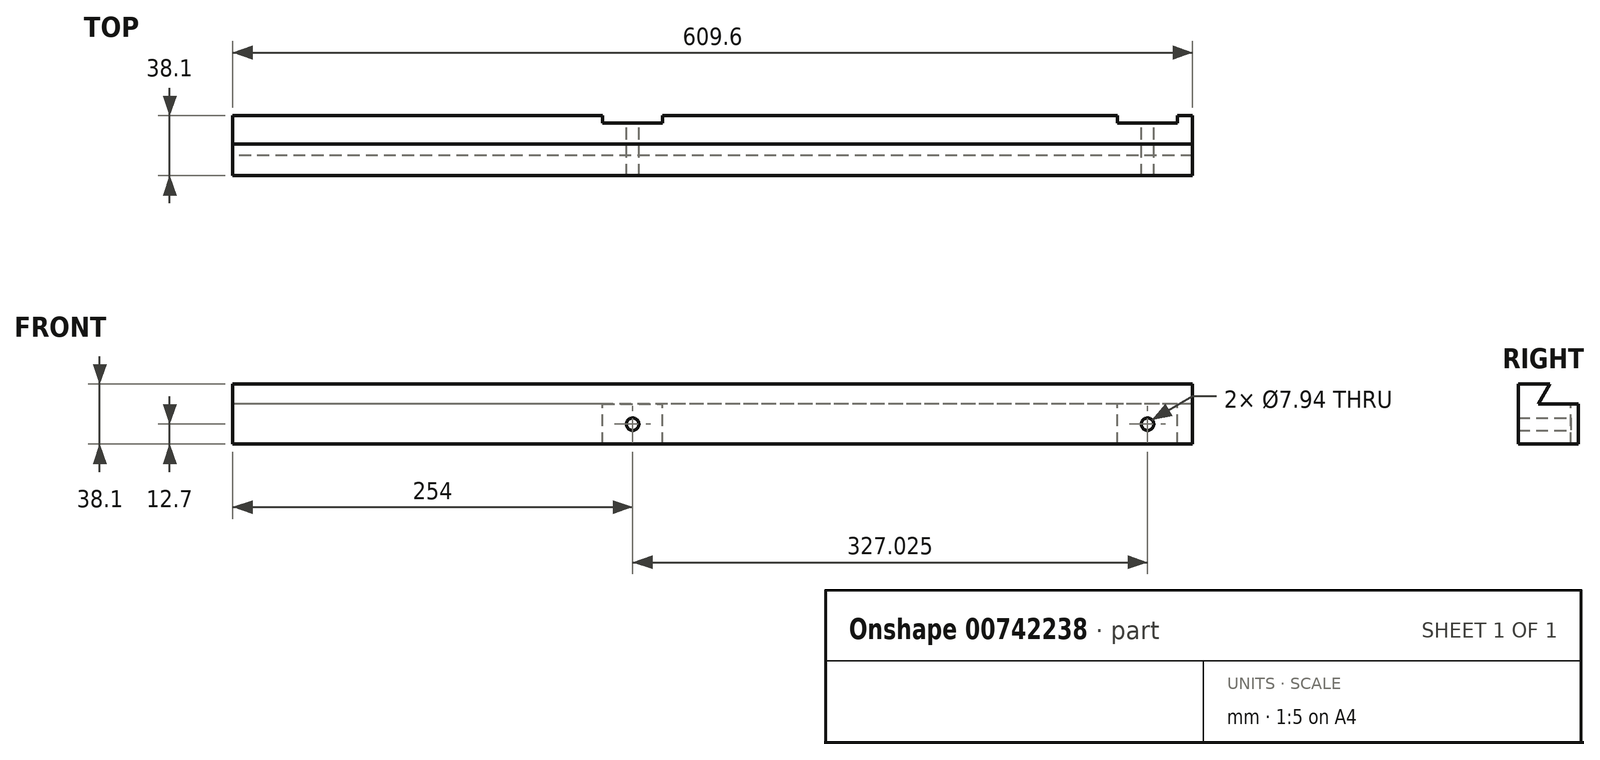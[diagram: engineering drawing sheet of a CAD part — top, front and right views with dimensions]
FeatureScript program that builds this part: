
annotation { "Feature Type Name" : "Feature", "Feature Type Description" : "" }
export const myFeature = defineFeature(function(context is Context, id is Id, definition is map)
    precondition{}
    {
        {
            var Q0;
            Q0=qCreatedBy(makeId("Right.planeOp"),FACE);
            var sketch = newSketch(context, id + "F0", { "sketchPlane" : qUnion([Q0])});
            skLineSegment(sketch, "E0", {"start": v(0, 0) * mm, "end": v(0, 38.1) * mm});
            skLineSegment(sketch, "E1", {"start": v(0, 38.1) * mm, "end": v(12.7, 38.1) * mm});
            skLineSegment(sketch, "E2", {"start": v(12.7, 38.1) * mm, "end": v(12.7, 25.4) * mm});
            skLineSegment(sketch, "E3", {"start": v(12.7, 25.4) * mm, "end": v(38.1, 25.4) * mm});
            skLineSegment(sketch, "E4", {"start": v(38.1, 25.4) * mm, "end": v(38.1, 0) * mm});
            skLineSegment(sketch, "E5", {"start": v(38.1, 0) * mm, "end": v(0, 0) * mm});
            skSolve(sketch);
        }
        {
            var Q0;
            Q0=makeQuery(id+"F0.imprint","IMPRINT",FACE,{"disambiguationData":[TD([[makeQuery(id+"F0.imprint","IMPRINT",EDGE,{"derivedFrom":sQuery(id+"F0.wireOp",EDGE,"E0")}),-1.0]])]});
            extrude(context, id + "F1", {"entities" : qUnion([Q0]), "depth" : 304.8 * mm, "offsetDistance" : 25.4 * mm, "hasSecondDirection" : true, "secondDirectionOppositeDirection" : true, "secondDirectionDepth" : 304.8 * mm});
        }
        {
            var Q0;
            Q0=makeQuery(id+"F1.opExtrude","SWEPT_FACE",FACE,{"disambiguationData":[OSD([sQuery(id+"F0.wireOp",EDGE,"E3")])]});
            var sketch = newSketch(context, id + "F2", { "sketchPlane" : qUnion([Q0])});
            skLineSegment(sketch, "E6", {"start": v(295.28, 38.1) * mm, "end": v(295.28, 33.34) * mm});
            skLineSegment(sketch, "E7", {"start": v(295.28, 33.34) * mm, "end": v(257.18, 33.34) * mm});
            skLineSegment(sketch, "E8", {"start": v(257.18, 33.34) * mm, "end": v(257.18, 38.1) * mm});
            skLineSegment(sketch, "E9", {"start": v(257.18, 38.1) * mm, "end": v(295.28, 38.1) * mm});
            skLineSegment(sketch, "E10", {"start": v(-69.85, 38.1) * mm, "end": v(-69.85, 33.34) * mm});
            skLineSegment(sketch, "E11", {"start": v(-69.85, 33.34) * mm, "end": v(-31.75, 33.34) * mm});
            skLineSegment(sketch, "E12", {"start": v(-31.75, 33.34) * mm, "end": v(-31.75, 38.1) * mm});
            skLineSegment(sketch, "E13", {"start": v(-31.75, 38.1) * mm, "end": v(-69.85, 38.1) * mm});
            skSolve(sketch);
        }
        {
            var Q0;
            Q0=makeQuery(id+"F2.imprint","IMPRINT",FACE,{"disambiguationData":[TD([[makeQuery(id+"F2.imprint","IMPRINT",EDGE,{"derivedFrom":sQuery(id+"F2.wireOp",EDGE,"E10")}),1.0]])]});
            var Q1;
            Q1=makeQuery(id+"F2.imprint","IMPRINT",FACE,{"disambiguationData":[TD([[makeQuery(id+"F2.imprint","IMPRINT",EDGE,{"derivedFrom":sQuery(id+"F2.wireOp",EDGE,"E6")}),-1.0]])]});
            extrude(context, id + "F3", {"entities" : qUnion([Q0, Q1]), "operationType" : NewBodyOperationType.REMOVE, "endBound" : BoundingType.THROUGH_ALL, "oppositeDirection" : true, "depth" : 25.4 * mm, "offsetDistance" : 25.4 * mm});
        }
        {
            var Q0;
            Q0=makeQuery(id+"F3.boolean.opBoolean","COPY",FACE,{"derivedFrom":makeQuery(id+"F3.opExtrude","SWEPT_FACE",FACE,{"disambiguationData":[OSD([sQuery(id+"F2.wireOp",EDGE,"E11")])]})});
            var sketch = newSketch(context, id + "F4", { "sketchPlane" : qUnion([Q0])});
            skPoint(sketch, "E14", {"position": v(-276.22, 12.7) * mm});
            skPoint(sketch, "E15", {"position": v(50.8, 12.7) * mm});
            skLineSegment(sketch, "E16", {"start": v(50.8, 25.4) * mm, "end": v(50.8, -27.74) * mm, "construction": true});
            skLineSegment(sketch, "E17", {"start": v(69.85, 12.7) * mm, "end": v(31.75, 12.7) * mm, "construction": true});
            skSolve(sketch);
        }
        {
            var Q0;
            Q0=sQuery(id+"F4.wireOp",VERTEX,"E14");
            var Q1;
            Q1=sQuery(id+"F4.wireOp",VERTEX,"E15");
            var Q2;
            Q2=makeQuery(id+"F1.opExtrude","SWEPT_BODY",BODY,{"disambiguationData":[OSD([sQuery(id+"F0.wireOp",EDGE,"E0"),sQuery(id+"F0.wireOp",EDGE,"E1"),sQuery(id+"F0.wireOp",EDGE,"E2"),sQuery(id+"F0.wireOp",EDGE,"E3"),sQuery(id+"F0.wireOp",EDGE,"E4"),sQuery(id+"F0.wireOp",EDGE,"E5")])]});
            hole(context, id + "F5", {"style" : HoleStyle.SIMPLE, "endStyle" : HoleEndStyle.THROUGH, "holeDiameter" : 7.94 * mm, "majorDiameter" : 6.35 * mm, "isTappedThrough" : true, "tappedDepth" : 12.7 * mm, "tapClearance" : 3, "locations" : qUnion([Q0, Q1]), "scope" : qUnion([Q2])});
        }
        {
            var Q0;
            Q0=makeQuery(id+"F1.opExtrude","CAP_FACE",FACE,{"disambiguationData":[OSD([sQuery(id+"F0.wireOp",EDGE,"E0"),sQuery(id+"F0.wireOp",EDGE,"E1"),sQuery(id+"F0.wireOp",EDGE,"E2"),sQuery(id+"F0.wireOp",EDGE,"E3"),sQuery(id+"F0.wireOp",EDGE,"E4"),sQuery(id+"F0.wireOp",EDGE,"E5")])],"isStart":false});
            var sketch = newSketch(context, id + "F6", { "sketchPlane" : qUnion([Q0])});
            skLineSegment(sketch, "E18", {"start": v(12.7, 38.1) * mm, "end": v(20.03, 38.1) * mm});
            skLineSegment(sketch, "E19", {"start": v(20.03, 38.1) * mm, "end": v(12.7, 25.4) * mm});
            skLineSegment(sketch, "E20", {"start": v(12.7, 25.4) * mm, "end": v(12.7, 38.1) * mm});
            skSolve(sketch);
        }
        {
            var Q0;
            Q0=makeQuery(id+"F6.imprint","IMPRINT",FACE,{"disambiguationData":[TD([[makeQuery(id+"F6.imprint","IMPRINT",EDGE,{"derivedFrom":sQuery(id+"F6.wireOp",EDGE,"E18")}),-1.0]])]});
            var Q1;
            Q1=makeQuery(id+"F1.opExtrude","CAP_FACE",FACE,{"disambiguationData":[OSD([sQuery(id+"F0.wireOp",EDGE,"E0"),sQuery(id+"F0.wireOp",EDGE,"E1"),sQuery(id+"F0.wireOp",EDGE,"E2"),sQuery(id+"F0.wireOp",EDGE,"E3"),sQuery(id+"F0.wireOp",EDGE,"E4"),sQuery(id+"F0.wireOp",EDGE,"E5")])],"isStart":true});
            extrude(context, id + "F7", {"entities" : qUnion([Q0]), "operationType" : NewBodyOperationType.ADD, "endBound" : BoundingType.UP_TO_SURFACE, "oppositeDirection" : true, "depth" : 25.4 * mm, "endBoundEntityFace" : qUnion([Q1]), "offsetDistance" : 25.4 * mm});
        }
    });
